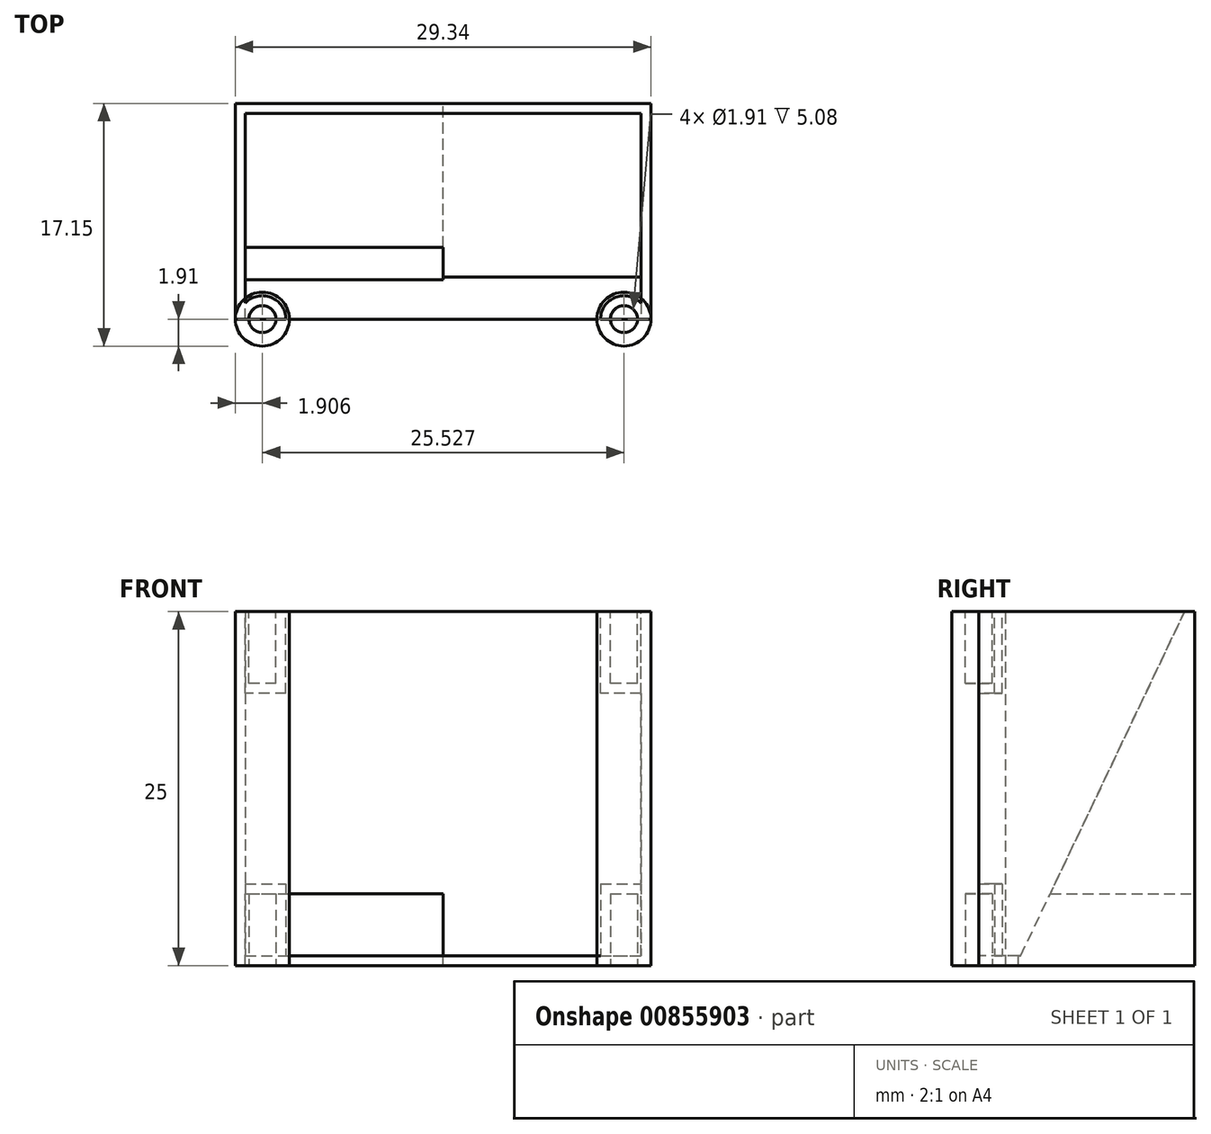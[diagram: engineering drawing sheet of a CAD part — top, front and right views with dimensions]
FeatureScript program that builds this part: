
annotation { "Feature Type Name" : "Feature", "Feature Type Description" : "" }
export const myFeature = defineFeature(function(context is Context, id is Id, definition is map)
    precondition{}
    {
        {
            var Q0;
            Q0=qCreatedBy(makeId("Front.planeOp"),FACE);
            var sketch = newSketch(context, id + "F0", { "sketchPlane" : qUnion([Q0])});
            skLineSegment(sketch, "E0.right", {"start": v(-10.86, 25) * mm, "end": v(-10.86, 0) * mm});
            skLineSegment(sketch, "E1.left", {"start": v(10.86, 0) * mm, "end": v(10.86, 25) * mm});
            skLineSegment(sketch, "E2", {"start": v(-12.76, 25) * mm, "end": v(-12.76, 0) * mm});
            skLineSegment(sketch, "E3", {"start": v(12.76, 25) * mm, "end": v(12.76, 0) * mm});
            skLineSegment(sketch, "E4", {"start": v(-12.76, 25) * mm, "end": v(-10.86, 25) * mm});
            skLineSegment(sketch, "E5", {"start": v(-12.76, 0) * mm, "end": v(-10.86, 0) * mm});
            skLineSegment(sketch, "E6", {"start": v(10.86, 0) * mm, "end": v(12.76, 0) * mm});
            skLineSegment(sketch, "E7", {"start": v(10.86, 25) * mm, "end": v(12.76, 25) * mm});
            skSolve(sketch);
        }
        {
            var Q0;
            Q0=makeQuery(id+"F0.imprint","IMPRINT",FACE,{"disambiguationData":[TD([[makeQuery(id+"F0.imprint","IMPRINT",EDGE,{"derivedFrom":sQuery(id+"F0.wireOp",EDGE,"E0.right")}),-1.0]])]});
            var Q1;
            Q1=sQuery(id+"F0.wireOp",EDGE,"E2");
            revolve(context, id + "F1", {"surfaceOperationType" : NewSurfaceOperationType.ADD, "entities" : qUnion([Q0]), "axis" : qUnion([Q1]), "revolveType" : RevolveType.FULL});
        }
        {
            var Q0;
            Q0=qCreatedBy(makeId("Front.planeOp"),FACE);
            var sketch = newSketch(context, id + "F2", { "sketchPlane" : qUnion([Q0])});
            skLineSegment(sketch, "E8.right", {"start": v(12.76, 25) * mm, "end": v(12.76, 0) * mm});
            skLineSegment(sketch, "E9", {"start": v(10.86, 25) * mm, "end": v(10.86, 0) * mm});
            skLineSegment(sketch, "E10", {"start": v(10.86, 25) * mm, "end": v(12.76, 25) * mm});
            skLineSegment(sketch, "E11", {"start": v(10.86, 0) * mm, "end": v(12.76, 0) * mm});
            skSolve(sketch);
        }
        {
            var Q0;
            Q0 = qSketchRegion(id + "F2", true);
            var Q1;
            Q1=sQuery(id+"F2.wireOp",EDGE,"E8.right");
            revolve(context, id + "F3", {"surfaceOperationType" : NewSurfaceOperationType.NEW, "entities" : qUnion([Q0]), "axis" : qUnion([Q1]), "revolveType" : RevolveType.FULL});
        }
        {
            var Q0;
            Q0=makeQuery(id+"F3.opRevolve","SWEPT_FACE",FACE,{"disambiguationData":[OSD([sQuery(id+"F2.wireOp",EDGE,"E11")])]});
            var sketch = newSketch(context, id + "F4", { "sketchPlane" : qUnion([Q0])});
            skCircle(sketch, "E12", {"center": v(12.76, 0) * mm, "radius": 0.95 * mm});
            skSolve(sketch);
        }
        {
            var Q0;
            Q0=makeQuery(id+"F3.opRevolve","SWEPT_FACE",FACE,{"disambiguationData":[OSD([sQuery(id+"F2.wireOp",EDGE,"E10")])]});
            var sketch = newSketch(context, id + "F5", { "sketchPlane" : qUnion([Q0])});
            skCircle(sketch, "E13", {"center": v(12.76, 0) * mm, "radius": 0.95 * mm});
            skSolve(sketch);
        }
        {
            var Q0;
            Q0=makeQuery(id+"F1.opRevolve","SWEPT_FACE",FACE,{"disambiguationData":[OSD([sQuery(id+"F0.wireOp",EDGE,"E4")])]});
            var sketch = newSketch(context, id + "F6", { "sketchPlane" : qUnion([Q0])});
            skCircle(sketch, "E14", {"center": v(-12.76, 0) * mm, "radius": 0.95 * mm});
            skSolve(sketch);
        }
        {
            var Q0;
            Q0=makeQuery(id+"F6.imprint","IMPRINT",FACE,{"disambiguationData":[TD([[makeQuery(id+"F6.imprint","IMPRINT",EDGE,{"derivedFrom":sQuery(id+"F6.wireOp",EDGE,"E14")}),-1.0]])]});
            var sketch = newSketch(context, id + "F7", { "sketchPlane" : qUnion([Q0])});
            skLineSegment(sketch, "E15", {"start": v(-12.77, 0) * mm, "end": v(-14.67, 0) * mm});
            skSolve(sketch);
        }
        {
            var Q0;
            Q0=makeQuery(id+"F1.opRevolve","SWEPT_FACE",FACE,{"disambiguationData":[OSD([sQuery(id+"F0.wireOp",EDGE,"E5")])]});
            var sketch = newSketch(context, id + "F8", { "sketchPlane" : qUnion([Q0])});
            skLineSegment(sketch, "E16", {"start": v(-12.76, 0) * mm, "end": v(-14.67, 0) * mm});
            skSolve(sketch);
        }
        {
            var Q0;
            Q0=qCreatedBy(makeId("Front.planeOp"),FACE);
            var sketch = newSketch(context, id + "F9", { "sketchPlane" : qUnion([Q0])});
            skLineSegment(sketch, "E17.bottom", {"start": v(-14.67, 25) * mm, "end": v(14.67, 25) * mm});
            skLineSegment(sketch, "E17.top", {"start": v(-14.67, 0) * mm, "end": v(14.67, 0) * mm});
            skLineSegment(sketch, "E17.left", {"start": v(-14.67, 25) * mm, "end": v(-14.67, 0) * mm});
            skLineSegment(sketch, "E17.right", {"start": v(14.67, 25) * mm, "end": v(14.67, 0) * mm});
            skSolve(sketch);
        }
        {
            var Q0;
            Q0 = qSketchRegion(id + "F9", true);
            extrude(context, id + "F10", {"entities" : qUnion([Q0]), "oppositeDirection" : true, "depth" : 15.24 * mm, "offsetDistance" : 25.4 * mm});
        }
        {
            var Q0;
            Q0=makeQuery(id+"F7.imprint","IMPRINT",FACE,{"disambiguationData":[TD([[makeQuery(id+"F7.imprint","IMPRINT",EDGE,{"derivedFrom":makeQuery(id+"F6.imprint","IMPRINT",EDGE,{"derivedFrom":sQuery(id+"F6.wireOp",EDGE,"E14")})}),1.0]])]});
            extrude(context, id + "F11", {"entities" : qUnion([Q0]), "operationType" : NewBodyOperationType.REMOVE, "oppositeDirection" : true, "depth" : 5.08 * mm, "offsetDistance" : 25.4 * mm});
        }
        {
            var Q0;
            Q0=makeQuery(id+"F5.imprint","IMPRINT",FACE,{"disambiguationData":[TD([[makeQuery(id+"F5.imprint","IMPRINT",EDGE,{"derivedFrom":sQuery(id+"F5.wireOp",EDGE,"E13")}),1.0]])]});
            extrude(context, id + "F12", {"entities" : qUnion([Q0]), "operationType" : NewBodyOperationType.REMOVE, "oppositeDirection" : true, "depth" : 5.08 * mm, "offsetDistance" : 25.4 * mm});
        }
        {
            var Q0;
            Q0=makeQuery(id+"F4.imprint","IMPRINT",FACE,{"disambiguationData":[TD([[makeQuery(id+"F4.imprint","IMPRINT",EDGE,{"derivedFrom":sQuery(id+"F4.wireOp",EDGE,"E12")}),1.0]])]});
            extrude(context, id + "F13", {"entities" : qUnion([Q0]), "operationType" : NewBodyOperationType.REMOVE, "oppositeDirection" : true, "depth" : 5.08 * mm, "offsetDistance" : 25.4 * mm});
        }
        {
            var Q0;
            Q0=makeQuery(id+"F8.imprint","IMPRINT",FACE,{"disambiguationData":[TD([[makeQuery(id+"F8.imprint","IMPRINT",EDGE,{"derivedFrom":makeQuery(id+"F1.opRevolve","SWEPT_EDGE",EDGE,{"disambiguationData":[OSD([sQuery(id+"F0.wireOp",EDGE,"E0.right"),sQuery(id+"F0.wireOp",EDGE,"E5")])]})}),-1.0]])]});
            var sketch = newSketch(context, id + "F14", { "sketchPlane" : qUnion([Q0])});
            skCircle(sketch, "E18", {"center": v(-12.76, 0) * mm, "radius": 0.95 * mm});
            skSolve(sketch);
        }
        {
            var Q0;
            Q0=makeQuery(id+"F14.imprint","IMPRINT",FACE,{"disambiguationData":[TD([[makeQuery(id+"F14.imprint","IMPRINT",EDGE,{"derivedFrom":sQuery(id+"F14.wireOp",EDGE,"E18")}),1.0]])]});
            extrude(context, id + "F15", {"entities" : qUnion([Q0]), "operationType" : NewBodyOperationType.REMOVE, "oppositeDirection" : true, "depth" : 5.08 * mm, "offsetDistance" : 25.4 * mm});
        }
        {
            var Q0;
            Q0=makeQuery(id+"F10.opExtrude","CAP_FACE",FACE,{"disambiguationData":[OSD([sQuery(id+"F9.wireOp",EDGE,"E17.bottom"),sQuery(id+"F9.wireOp",EDGE,"E17.top"),sQuery(id+"F9.wireOp",EDGE,"E17.left"),sQuery(id+"F9.wireOp",EDGE,"E17.right")])],"isStart":true});
            var Q1;
            Q1=makeQuery(id+"F10.opExtrude","SWEPT_FACE",FACE,{"disambiguationData":[OSD([sQuery(id+"F9.wireOp",EDGE,"E17.bottom")])]});
            var Q2;
            Q2=makeQuery(id+"F10.opExtrude","SWEPT_BODY",BODY,{"disambiguationData":[OSD([sQuery(id+"F9.wireOp",EDGE,"E17.bottom"),sQuery(id+"F9.wireOp",EDGE,"E17.top"),sQuery(id+"F9.wireOp",EDGE,"E17.left"),sQuery(id+"F9.wireOp",EDGE,"E17.right")])]});
            shell(context, id + "F16", {"entities" : qUnion([Q0, Q1]), "parts" : qUnion([Q2]), "thickness" : .7 * mm});
        }
        {
            var Q0;
            Q0=makeQuery(id+"F16.opShell","OFFSET_FACE",FACE,{"disambiguationData":[OSD([sQuery(id+"F9.wireOp",EDGE,"E17.right")])]});
            var sketch = newSketch(context, id + "F17", { "sketchPlane" : qUnion([Q0])});
            skLineSegment(sketch, "E19", {"start": v(-1.94, 0.7) * mm, "end": v(-2.97, 0.7) * mm});
            skLineSegment(sketch, "E20", {"start": v(-2.97, 0.7) * mm, "end": v(-14.54, 25) * mm});
            skSolve(sketch);
        }
        {
            var Q0;
            {var subQ0=sQuery(id+"F17.wireOp",EDGE,"E20");Q0=makeQuery(id+"F17.imprint","IMPRINT",FACE,{"disambiguationData":[TD([[makeQuery(id+"F17.imprint","IMPRINT",EDGE,{"derivedFrom":subQ0}),1.0]])]});}
            extrude(context, id + "F18", {"entities" : qUnion([Q0]), "operationType" : NewBodyOperationType.ADD, "depth" : 28.32 * mm, "offsetDistance" : 25.4 * mm});
        }
        {
            var Q0;
            Q0=makeQuery(id+"F10.opExtrude","CAP_FACE",FACE,{"disambiguationData":[OSD([sQuery(id+"F9.wireOp",EDGE,"E17.bottom"),sQuery(id+"F9.wireOp",EDGE,"E17.top"),sQuery(id+"F9.wireOp",EDGE,"E17.left"),sQuery(id+"F9.wireOp",EDGE,"E17.right")])],"isStart":false});
            var sketch = newSketch(context, id + "F19", { "sketchPlane" : qUnion([Q0])});
            skLineSegment(sketch, "E21.bottom", {"start": v(13.97, 0) * mm, "end": v(0, 0) * mm});
            skLineSegment(sketch, "E21.top", {"start": v(13.97, 5.08) * mm, "end": v(0, 5.08) * mm});
            skLineSegment(sketch, "E21.left", {"start": v(13.97, 0) * mm, "end": v(13.97, 5.08) * mm});
            skLineSegment(sketch, "E21.right", {"start": v(0, 0) * mm, "end": v(0, 5.08) * mm});
            skSolve(sketch);
        }
        {
            var Q0;
            Q0 = qSketchRegion(id + "F19", true);
            extrude(context, id + "F20", {"entities" : qUnion([Q0]), "operationType" : NewBodyOperationType.REMOVE, "oppositeDirection" : true, "depth" : 12.45 * mm, "offsetDistance" : 25.4 * mm});
        }
    });
